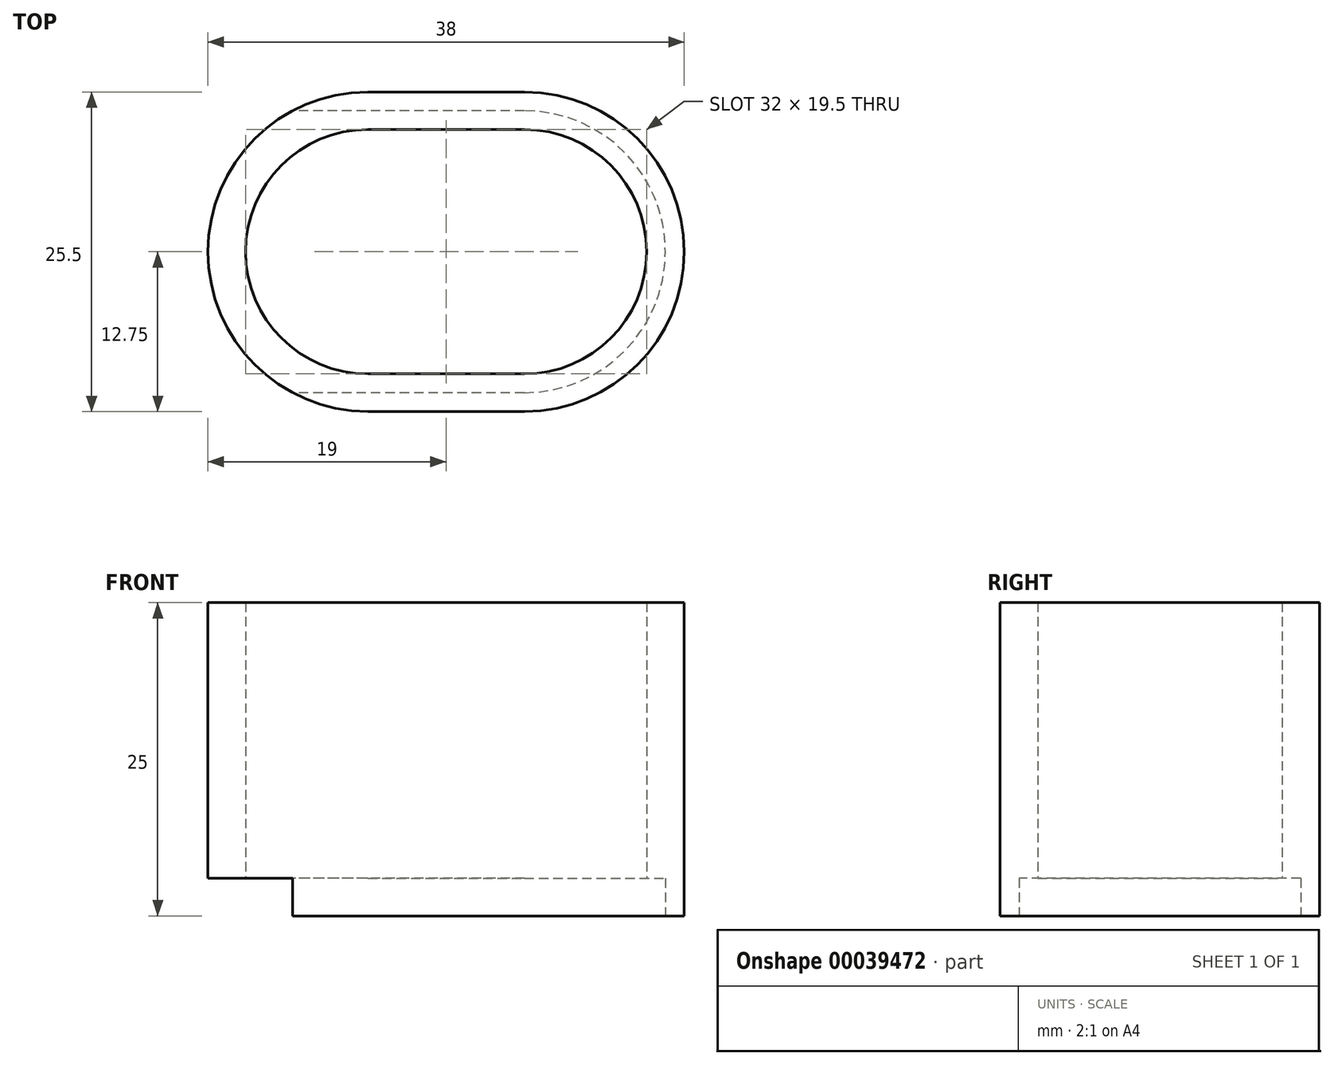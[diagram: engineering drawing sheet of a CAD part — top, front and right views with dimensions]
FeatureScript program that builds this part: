
annotation { "Feature Type Name" : "Feature", "Feature Type Description" : "" }
export const myFeature = defineFeature(function(context is Context, id is Id, definition is map)
    precondition{}
    {
        {
            var Q0;
            Q0=qCreatedBy(makeId("Top.planeOp"),FACE);
            var sketch = newSketch(context, id + "F0", { "sketchPlane" : qUnion([Q0])});
            skLineSegment(sketch, "E0.rect.bottom", {"start": v(19, -12.75) * mm, "end": v(-19, -12.75) * mm});
            skLineSegment(sketch, "E0.rect.top", {"start": v(19, 12.75) * mm, "end": v(-19, 12.75) * mm});
            skLineSegment(sketch, "E0.rect.left", {"start": v(19, -12.75) * mm, "end": v(19, 12.75) * mm});
            skLineSegment(sketch, "E0.rect.right", {"start": v(-19, -12.75) * mm, "end": v(-19, 12.75) * mm});
            skPoint(sketch, "E0.rect.middle", {"position": v(0, 0) * mm});
            skCircle(sketch, "E1", {"center": v(-6.25, 0) * mm, "radius": 12.75 * mm});
            skCircle(sketch, "E2", {"center": v(6.25, 0) * mm, "radius": 12.75 * mm});
            skSolve(sketch);
        }
        {
            var Q0;
            Q0=qCreatedBy(makeId("Top.planeOp"),FACE);
            var sketch = newSketch(context, id + "F1", { "sketchPlane" : qUnion([Q0])});
            skLineSegment(sketch, "E3.0.1", {"start": v(6.25, 12.75) * mm, "end": v(-6.25, 12.75) * mm});
            skArc(sketch, "E3.1.2", {"start": v(6.25, -12.75) * mm, "mid": v(15.27, -9.02) * mm, "end": v(19, 0) * mm});
            skArc(sketch, "E3.1.3", {"start": v(19, 0) * mm, "mid": v(15.27, 9.02) * mm, "end": v(6.25, 12.75) * mm});
            skArc(sketch, "E3.2.2", {"start": v(-6.25, 12.75) * mm, "mid": v(-15.27, 9.02) * mm, "end": v(-19, 0) * mm});
            skArc(sketch, "E3.2.3", {"start": v(-19, 0) * mm, "mid": v(-15.27, -9.02) * mm, "end": v(-6.25, -12.75) * mm});
            skLineSegment(sketch, "E3.4.0", {"start": v(-6.25, -12.75) * mm, "end": v(6.25, -12.75) * mm});
            skArc(sketch, "E4.0", {"start": v(6.25, -9.75) * mm, "mid": v(13.14, -6.9) * mm, "end": v(16, 0) * mm});
            skLineSegment(sketch, "E4.1", {"start": v(6.25, 9.75) * mm, "end": v(-6.25, 9.75) * mm});
            skArc(sketch, "E4.2", {"start": v(-6.25, 9.75) * mm, "mid": v(-13.14, 6.9) * mm, "end": v(-16, 0) * mm});
            skArc(sketch, "E4.3", {"start": v(16, 0) * mm, "mid": v(13.14, 6.9) * mm, "end": v(6.25, 9.75) * mm});
            skArc(sketch, "E4.4", {"start": v(-16, 0) * mm, "mid": v(-13.14, -6.9) * mm, "end": v(-6.25, -9.75) * mm});
            skLineSegment(sketch, "E4.5", {"start": v(-6.25, -9.75) * mm, "end": v(6.25, -9.75) * mm});
            skSolve(sketch);
        }
        {
            var Q0;
            Q0=makeQuery(id+"F1.imprint","IMPRINT",FACE,{"disambiguationData":[TD([[makeQuery(id+"F1.imprint","IMPRINT",EDGE,{"derivedFrom":sQuery(id+"F1.wireOp",EDGE,"E3.0.1")}),1.0]])]});
            extrude(context, id + "F2", {"entities" : qUnion([Q0]), "depth" : 25 * mm});
        }
        {
            var Q0;
            Q0=qCreatedBy(makeId("Top.planeOp"),FACE);
            var sketch = newSketch(context, id + "F3", { "sketchPlane" : qUnion([Q0])});
            skArc(sketch, "E5.0", {"start": v(6.25, -9.75) * mm, "mid": v(16, 0) * mm, "end": v(6.25, 9.75) * mm});
            skLineSegment(sketch, "E5.1", {"start": v(6.25, 9.75) * mm, "end": v(-21.7, 9.75) * mm});
            skLineSegment(sketch, "E5.2", {"start": v(-6.25, -9.75) * mm, "end": v(6.25, -9.75) * mm});
            skPoint(sketch, "E6.orphan", {"position": v(-6.25, 9.75) * mm});
            skLineSegment(sketch, "E7", {"start": v(-21.7, 13.97) * mm, "end": v(-21.7, -16.36) * mm});
            skLineSegment(sketch, "E8", {"start": v(-6.25, -9.75) * mm, "end": v(-21.7, -9.75) * mm});
            skLineSegment(sketch, "E9.0", {"start": v(6.25, 11.25) * mm, "end": v(-21.7, 11.25) * mm});
            skArc(sketch, "E9.1", {"start": v(6.25, -11.25) * mm, "mid": v(17.5, 0) * mm, "end": v(6.25, 11.25) * mm});
            skLineSegment(sketch, "E9.2", {"start": v(-6.25, -11.25) * mm, "end": v(6.25, -11.25) * mm});
            skLineSegment(sketch, "E9.3", {"start": v(-6.25, -11.25) * mm, "end": v(-21.7, -11.25) * mm});
            skSolve(sketch);
        }
        {
            var Q0;
            Q0=makeQuery(id+"F3.imprint","IMPRINT",FACE,{"disambiguationData":[TD([[makeQuery(id+"F3.imprint","IMPRINT",EDGE,{"derivedFrom":sQuery(id+"F3.wireOp",EDGE,"E5.0")}),-1.0]])]});
            var Q1;
            Q1=makeQuery(id+"F3.imprint","IMPRINT",FACE,{"disambiguationData":[TD([[makeQuery(id+"F3.imprint","IMPRINT",EDGE,{"derivedFrom":sQuery(id+"F3.wireOp",EDGE,"E5.0")}),1.0]])]});
            extrude(context, id + "F4", {"entities" : qUnion([Q0, Q1]), "operationType" : NewBodyOperationType.REMOVE, "depth" : 3 * mm});
        }
    });
